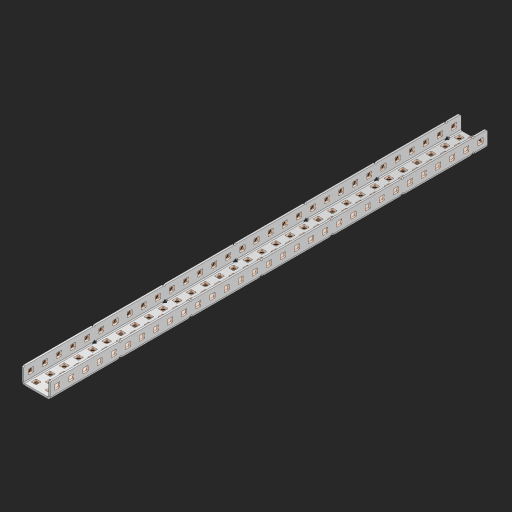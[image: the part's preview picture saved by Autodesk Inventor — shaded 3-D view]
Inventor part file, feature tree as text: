
AUTODESK INVENTOR PART (.ipt)
format: ipt  version: 2023 (Build 270158000, 158)  size: 1,936,896 bytes
history: native  units: in
note: dims shown in document units (in); Inventor stores cm internally (conversion verified against a paired STEP export)
features: other x162, extrude x153, sheet_metal_op x11, sketch x10, pattern_linear x2, mirror x1, chamfer x1
ambient origin geometry x8: Origin, YZ Plane, XZ Plane, XY Plane, X Axis, Y Axis, Z Axis, Center Point
bodies: Solid1 (feature_tree), Body (feature_tree)
feature tree (340):
  sheet_metal_op  "Flanges"
  other  "Flange Pattern Plane"
  other  "Flange Pattern Sketch"
  sheet_metal_op  "Flange Pattern"
  sheet_metal_op  "Body Pattern"
  pattern_linear  "Center Pattern"  Spacing1=0.0625in  [1 undecoded]
  other  "Arc Length"
  mirror  "Notch Mirror"
  pattern_linear  "Notch Pattern"  Spacing1=0.182in  [1 undecoded]
  chamfer  "End Chamfer"
  extrude  "Half Cut"  Depth=0.02in
  sketch  "Sketch1"  dims[d0=1.0in]
  other  "Plate1"
  sketch  "Sketch2"  dims[d1=15.5in]
  other  "Plate2"
  sheet_metal_op  "Bend1"
  sheet_metal_op  "Corner1"
  sketch  "Sketch3"  dims[d2=0.0625in]
  sketch  "Sketch7"  dims[d3=0.0625in]
  other  "Srf1"
  other  "Srf2"
  sketch  "Sketch8"  dims[d4=0.0312in]
  sketch  "Sketch9"  dims[d5=0.125in]
  other  "Srf91"
  sheet_metal_op  "Body Pattern Sketch"
  other  "Srf92"
  sketch  "Sketch13"  dims[d6=0.0625in]
  sketch  "Sketch14"  dims[d7=0.5in d8=90.0deg d9=0.0312in]
  sketch  "Sketch15"  dims[d10=0.25in]
  sketch  "Sketch16"  dims[d11=0.0625in d12=0.0625in d16=0.182in d17=0.02in d18=0.0625in d19=0.0in d20=0.25in d21=0.25in d38=12.2047in d40=0.5in d41=0.7874in d43=1.0in d46=0.172in d47=1.0in d48=0.0in d49=0.182in d50=0.02in d51=0.25in d52=0.25in d53=0.0625in d54=0.0in d55=0.172in d56=1.0in d57=0.0in d58=0.25in d60=12.2047in d62=0.5in d63=0.7874in d65=0.5in d85=0.1473in d86=0.1782in d88=0.04in d89=0.0625in d90=0.0in d91=0.04in d92=0.0491in d95=2.5in d96=0.04in d97=0.25in d98=45.0deg d99=0.25in d100=0.5in d101=0.0in d102=2.497in d106=0.182in d107=0.02in d108=0.5in d109=0.5in d110=0.0625in d111=0.0in d112=0.172in d113=0.5in d114=0.0in d117=0.5in d118=0.5in d119=0.5in]
  other  "Srf786"
  other  "Srf823"
  other  "Srf824"
  other  "Srf825"
  other  "Srf826"
  other  "Srf827"
  other  "Srf828"
  other  "Srf829"
  other  "Srf856"
  other  "Srf857"
  other  "Srf858"
  other  "Srf859"
  other  "Srf860"
  other  "Srf861"
  other  "Srf862"
  other  "Srf889"
  other  "Srf890"
  other  "Srf891"
  other  "Srf892"
  other  "Srf893"
  other  "Srf894"
  other  "Srf895"
  other  "Srf896"
  other  "Srf922"
  other  "Srf923"
  other  "Srf924"
  other  "Srf925"
  other  "Srf926"
  other  "Srf959"
  other  "Srf960"
  other  "Srf961"
  other  "Srf962"
  other  "Srf963"
  other  "Srf996"
  other  "Srf997"
  other  "Srf998"
  other  "Srf999"
  other  "Srf1000"
  other  "Srf1143"
  other  "Srf1144"
  other  "Srf1145"
  other  "Srf1146"
  other  "Srf1147"
  other  "Srf1148"
  other  "Srf1149"
  other  "Srf1150"
  other  "Srf1151"
  other  "Srf1152"
  other  "Srf1153"
  other  "Srf1154"
  other  "Srf1155"
  other  "Srf1156"
  other  "Srf1157"
  other  "Srf1158"
  other  "Srf1159"
  other  "Srf1160"
  other  "Srf1161"
  other  "Srf1162"
  other  "Srf1163"
  other  "Srf1164"
  other  "Srf1165"
  other  "Srf1166"
  other  "Srf1167"
  other  "Srf1168"
  other  "Srf1169"
  other  "Srf1170"
  other  "Srf1171"
  other  "Srf1172"
  other  "Srf1173"
  other  "Srf1174"
  other  "Srf1175"
  other  "Srf1176"
  other  "Srf1177"
  other  "Srf1178"
  other  "Srf1179"
  other  "Srf1180"
  other  "Srf1181"
  other  "Srf1182"
  other  "Srf1183"
  other  "Srf1184"
  other  "Srf1185"
  other  "Srf1186"
  other  "Srf1187"
  other  "Srf1188"
  other  "Srf1189"
  other  "Srf1190"
  other  "Srf1199"
  other  "Srf1200"
  other  "Srf1201"
  other  "Srf1202"
  other  "Srf1203"
  other  "Srf1204"
  other  "Srf1205"
  other  "Srf1206"
  other  "Srf1207"
  other  "Srf1208"
  other  "Srf1209"
  other  "Srf1210"
  other  "Srf1211"
  other  "Srf1212"
  other  "Srf1213"
  other  "Srf1214"
  other  "Srf1215"
  other  "Srf1216"
  other  "Srf1217"
  other  "Srf1218"
  other  "Srf1219"
  other  "Srf1220"
  other  "Srf1221"
  other  "Srf1222"
  other  "Srf1223"
  other  "Srf1224"
  other  "Srf1225"
  other  "Srf1226"
  other  "Srf1227"
  other  "Srf1228"
  other  "Srf1229"
  other  "Srf1230"
  other  "Srf1231"
  other  "Srf1232"
  other  "Srf1233"
  other  "Srf1234"
  other  "Srf1235"
  other  "Srf1236"
  other  "Srf1237"
  other  "Srf1238"
  other  "Srf1239"
  other  "Srf1240"
  other  "Srf1241"
  other  "Srf1242"
  other  "Srf1243"
  other  "Srf1244"
  other  "Srf1245"
  other  "Srf1246"
  other  "Srf1255"
  other  "Srf1256"
  other  "Srf1257"
  other  "Srf1258"
  other  "Srf1259"
  other  "Srf1260"
  other  "Srf1261"
  other  "Srf1262"
  other  "Srf1263"
  other  "Srf1264"
  other  "Srf1265"
  other  "Srf1266"
  other  "Srf1267"
  other  "Srf1268"
  other  "Srf1269"
  other  "Srf1270"
  other  "Srf1271"
  sheet_metal_op  "Flange Stamp"
  sheet_metal_op  "Flange Circle"
  sheet_metal_op  "Body Stamp"
  sheet_metal_op  "Body Circle"
  other  "Center Stamp"
  other  "Center Circle"
  sheet_metal_op  "Notch"
  extrude  "ExtrusionSrf2"  Depth=0.0625in
  extrude  "ExtrusionSrf92"  TaperAngle=0.0deg  [1 undecoded]
  extrude  "ExtrusionSrf823"  Depth=0.5in
  extrude  "ExtrusionSrf824"  Depth=0.5in
  extrude  "ExtrusionSrf825"  Depth=0.5in
  extrude  "ExtrusionSrf826"  Depth=0.5in
  extrude  "ExtrusionSrf827"  Depth=1.0in TaperAngle=0.0deg
  extrude  "ExtrusionSrf828"  Depth=0.5in
  extrude  "ExtrusionSrf829"  Depth=0.02in
  extrude  "ExtrusionSrf856"  Depth=0.5in
  extrude  "ExtrusionSrf857"  Depth=0.5in
  extrude  "ExtrusionSrf858"  Depth=0.0625in
  extrude  "ExtrusionSrf859"  TaperAngle=0.0deg  [1 undecoded]
  extrude  "ExtrusionSrf860"  Depth=0.5in
  extrude  "ExtrusionSrf861"  Depth=1.0in TaperAngle=0.0deg
  extrude  "ExtrusionSrf862"  Depth=0.5in
  extrude  "ExtrusionSrf889"  Depth=0.5in
  extrude  "ExtrusionSrf890"  Depth=0.5in
  extrude  "ExtrusionSrf891"  Depth=0.5in
  extrude  "ExtrusionSrf892"  Depth=0.5in
  extrude  "ExtrusionSrf893"  Depth=0.5in
  extrude  "ExtrusionSrf894"  Depth=0.0625in
  extrude  "ExtrusionSrf895"  TaperAngle=0.0deg  [1 undecoded]
  extrude  "ExtrusionSrf896"  Depth=0.5in
  extrude  "ExtrusionSrf922"  Depth=0.5in
  extrude  "ExtrusionSrf923"  Depth=2.5in
  extrude  "ExtrusionSrf924"  Depth=0.5in TaperAngle=45.0deg
  extrude  "ExtrusionSrf925"  Depth=0.5in
  extrude  "ExtrusionSrf926"  Depth=0.5in TaperAngle=0.0deg
  extrude  "ExtrusionSrf959"  Depth=0.5in
  extrude  "ExtrusionSrf960"  Depth=0.5in
  extrude  "ExtrusionSrf961"  Depth=0.02in
  extrude  "ExtrusionSrf962"  Depth=0.5in
  extrude  "ExtrusionSrf963"  Depth=0.5in
  extrude  "ExtrusionSrf996"  Depth=0.0625in
  extrude  "ExtrusionSrf997"  TaperAngle=0.0deg  [1 undecoded]
  extrude  "ExtrusionSrf998"  Depth=0.5in
  extrude  "ExtrusionSrf999"  Depth=0.5in TaperAngle=0.0deg
  extrude  "ExtrusionSrf1000"  Depth=0.5in
  extrude  "ExtrusionSrf1143"  Depth=0.5in
  extrude  "ExtrusionSrf1144"  Depth=0.5in
  extrude  "ExtrusionSrf1145"  [1 undecoded]
  extrude  "ExtrusionSrf1146"  [1 undecoded]
  extrude  "ExtrusionSrf1147"  [1 undecoded]
  extrude  "ExtrusionSrf1148"  [1 undecoded]
  extrude  "ExtrusionSrf1149"  [1 undecoded]
  extrude  "ExtrusionSrf1150"  [1 undecoded]
  extrude  "ExtrusionSrf1151"  [1 undecoded]
  extrude  "ExtrusionSrf1152"  [1 undecoded]
  extrude  "ExtrusionSrf1153"  [1 undecoded]
  extrude  "ExtrusionSrf1154"  [1 undecoded]
  extrude  "ExtrusionSrf1155"  [1 undecoded]
  extrude  "ExtrusionSrf1156"  [1 undecoded]
  extrude  "ExtrusionSrf1157"  [1 undecoded]
  extrude  "ExtrusionSrf1158"  [1 undecoded]
  extrude  "ExtrusionSrf1159"  [1 undecoded]
  extrude  "ExtrusionSrf1160"  [1 undecoded]
  extrude  "ExtrusionSrf1161"  [1 undecoded]
  extrude  "ExtrusionSrf1162"  [1 undecoded]
  extrude  "ExtrusionSrf1163"  [1 undecoded]
  extrude  "ExtrusionSrf1164"  [1 undecoded]
  extrude  "ExtrusionSrf1165"  [1 undecoded]
  extrude  "ExtrusionSrf1166"  [1 undecoded]
  extrude  "ExtrusionSrf1167"  [1 undecoded]
  extrude  "ExtrusionSrf1168"  [1 undecoded]
  extrude  "ExtrusionSrf1169"  [1 undecoded]
  extrude  "ExtrusionSrf1170"  [1 undecoded]
  extrude  "ExtrusionSrf1171"  [1 undecoded]
  extrude  "ExtrusionSrf1172"  [1 undecoded]
  extrude  "ExtrusionSrf1173"  [1 undecoded]
  extrude  "ExtrusionSrf1174"  [1 undecoded]
  extrude  "ExtrusionSrf1175"  [1 undecoded]
  extrude  "ExtrusionSrf1176"  [1 undecoded]
  extrude  "ExtrusionSrf1177"  [1 undecoded]
  extrude  "ExtrusionSrf1178"  [1 undecoded]
  extrude  "ExtrusionSrf1179"  [1 undecoded]
  extrude  "ExtrusionSrf1180"  [1 undecoded]
  extrude  "ExtrusionSrf1181"  [1 undecoded]
  extrude  "ExtrusionSrf1182"  [1 undecoded]
  extrude  "ExtrusionSrf1183"  [1 undecoded]
  extrude  "ExtrusionSrf1184"  [1 undecoded]
  extrude  "ExtrusionSrf1185"  [1 undecoded]
  extrude  "ExtrusionSrf1186"  [1 undecoded]
  extrude  "ExtrusionSrf1187"  [1 undecoded]
  extrude  "ExtrusionSrf1188"  [1 undecoded]
  extrude  "ExtrusionSrf1189"  [1 undecoded]
  extrude  "ExtrusionSrf1190"  [1 undecoded]
  extrude  "ExtrusionSrf1199"  [1 undecoded]
  extrude  "ExtrusionSrf1200"  [1 undecoded]
  extrude  "ExtrusionSrf1201"  [1 undecoded]
  extrude  "ExtrusionSrf1202"  [1 undecoded]
  extrude  "ExtrusionSrf1203"  [1 undecoded]
  extrude  "ExtrusionSrf1204"  [1 undecoded]
  extrude  "ExtrusionSrf1205"  [1 undecoded]
  extrude  "ExtrusionSrf1206"  [1 undecoded]
  extrude  "ExtrusionSrf1207"  [1 undecoded]
  extrude  "ExtrusionSrf1208"  [1 undecoded]
  extrude  "ExtrusionSrf1209"  [1 undecoded]
  extrude  "ExtrusionSrf1210"  [1 undecoded]
  extrude  "ExtrusionSrf1211"  [1 undecoded]
  extrude  "ExtrusionSrf1212"  [1 undecoded]
  extrude  "ExtrusionSrf1213"  [1 undecoded]
  extrude  "ExtrusionSrf1214"  [1 undecoded]
  extrude  "ExtrusionSrf1215"  [1 undecoded]
  extrude  "ExtrusionSrf1216"  [1 undecoded]
  extrude  "ExtrusionSrf1217"  [1 undecoded]
  extrude  "ExtrusionSrf1218"  [1 undecoded]
  extrude  "ExtrusionSrf1219"  [1 undecoded]
  extrude  "ExtrusionSrf1220"  [1 undecoded]
  extrude  "ExtrusionSrf1221"  [1 undecoded]
  extrude  "ExtrusionSrf1222"  [1 undecoded]
  extrude  "ExtrusionSrf1223"  [1 undecoded]
  extrude  "ExtrusionSrf1224"  [1 undecoded]
  extrude  "ExtrusionSrf1225"  [1 undecoded]
  extrude  "ExtrusionSrf1226"  [1 undecoded]
  extrude  "ExtrusionSrf1227"  [1 undecoded]
  extrude  "ExtrusionSrf1228"  [1 undecoded]
  extrude  "ExtrusionSrf1229"  [1 undecoded]
  extrude  "ExtrusionSrf1230"  [1 undecoded]
  extrude  "ExtrusionSrf1231"  [1 undecoded]
  extrude  "ExtrusionSrf1232"  [1 undecoded]
  extrude  "ExtrusionSrf1233"  [1 undecoded]
  extrude  "ExtrusionSrf1234"  [1 undecoded]
  extrude  "ExtrusionSrf1235"  [1 undecoded]
  extrude  "ExtrusionSrf1236"  [1 undecoded]
  extrude  "ExtrusionSrf1237"  [1 undecoded]
  extrude  "ExtrusionSrf1238"  [1 undecoded]
  extrude  "ExtrusionSrf1239"  [1 undecoded]
  extrude  "ExtrusionSrf1240"  [1 undecoded]
  extrude  "ExtrusionSrf1241"  [1 undecoded]
  extrude  "ExtrusionSrf1242"  [1 undecoded]
  extrude  "ExtrusionSrf1243"  [1 undecoded]
  extrude  "ExtrusionSrf1244"  [1 undecoded]
  extrude  "ExtrusionSrf1245"  [1 undecoded]
  extrude  "ExtrusionSrf1246"  [1 undecoded]
  extrude  "ExtrusionSrf1255"  [1 undecoded]
  extrude  "ExtrusionSrf1256"  [1 undecoded]
  extrude  "ExtrusionSrf1257"  [1 undecoded]
  extrude  "ExtrusionSrf1258"  [1 undecoded]
  extrude  "ExtrusionSrf1259"  [1 undecoded]
  extrude  "ExtrusionSrf1260"  [1 undecoded]
  extrude  "ExtrusionSrf1261"  [1 undecoded]
  extrude  "ExtrusionSrf1262"  [1 undecoded]
  extrude  "ExtrusionSrf1263"  [1 undecoded]
  extrude  "ExtrusionSrf1264"  [1 undecoded]
  extrude  "ExtrusionSrf1265"  [1 undecoded]
  extrude  "ExtrusionSrf1266"  [1 undecoded]
  extrude  "ExtrusionSrf1267"  [1 undecoded]
  extrude  "ExtrusionSrf1268"  [1 undecoded]
  extrude  "ExtrusionSrf1269"  [1 undecoded]
  extrude  "ExtrusionSrf1270"  [1 undecoded]
  extrude  "ExtrusionSrf1271"  [1 undecoded]
note: 117 required parameter values undecoded (feature->parameter linkage not recoverable at this tier; creation-order binding heuristic only, values carry confidence <= 0.55)
